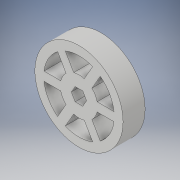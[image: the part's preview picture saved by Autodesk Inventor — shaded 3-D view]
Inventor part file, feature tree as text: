
AUTODESK INVENTOR PART (.ipt)
format: ipt  version: 2018 (Build 220112000, 112)  size: 173,056 bytes
history: native  units: in
note: dims shown in document units (in); Inventor stores cm internally (conversion verified against a paired STEP export)
features: extrude x1, sketch x1
ambient origin geometry x8: Origin, YZ Plane, XZ Plane, XY Plane, X Axis, Y Axis, Z Axis, Center Point
bodies: Solid1 (feature_tree)
feature tree (2):
  extrude  "Extrusion1"  Depth=0.5in
  sketch  "Sketch1"  dims[d0=0.3in d1=0.85in d2=2.0in d3=0.2in d4=120.0deg d5=120.0deg d6=120.0deg d7=120.0deg d8=0.2in d9=0.1in d10=0.2in d11=0.1in d13=0.1in d14=0.2in d15=0.2in d17=0.1in d18=0.1in d19=0.1in d20=0.2in d21=0.1in d22=0.5in d23=0.0in]
